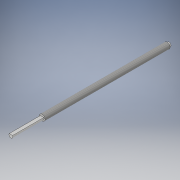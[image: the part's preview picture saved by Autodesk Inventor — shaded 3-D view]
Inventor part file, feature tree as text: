
AUTODESK INVENTOR PART (.ipt)
format: ipt  version: 2019.1 (Build 231200000, 200)  size: 109,056 bytes
history: native  units: in
note: dims shown in document units (in); Inventor stores cm internally (conversion verified against a paired STEP export)
features: extrude x3, sketch x3, thread x1
ambient origin geometry x8: Origin, YZ Plane, XZ Plane, XY Plane, X Axis, Y Axis, Z Axis, Center Point
bodies: Solid1 (feature_tree)
feature tree (7):
  extrude  "Extrusion1"  Depth=10.0in TaperAngle=0.0deg
  thread  "Thread1"  [1 undecoded]
  extrude  "Extrusion2"  Depth=0.0625in
  extrude  "Extrusion3"  Depth=0.125in
  sketch  "Sketch1"  dims[d0=0.375in d1=10.0in d2=0.0in d3=1.0in d4=0.0in]
  sketch  "Sketch2"  dims[d5=0.25in d6=0.0625in]
  sketch  "Sketch4"  dims[d7=2.0in d8=0.0in d16=0.25in d17=0.125in d18=0.0in]
note: 1 required parameter value undecoded (feature->parameter linkage not recoverable at this tier; creation-order binding heuristic only, values carry confidence <= 0.55)
